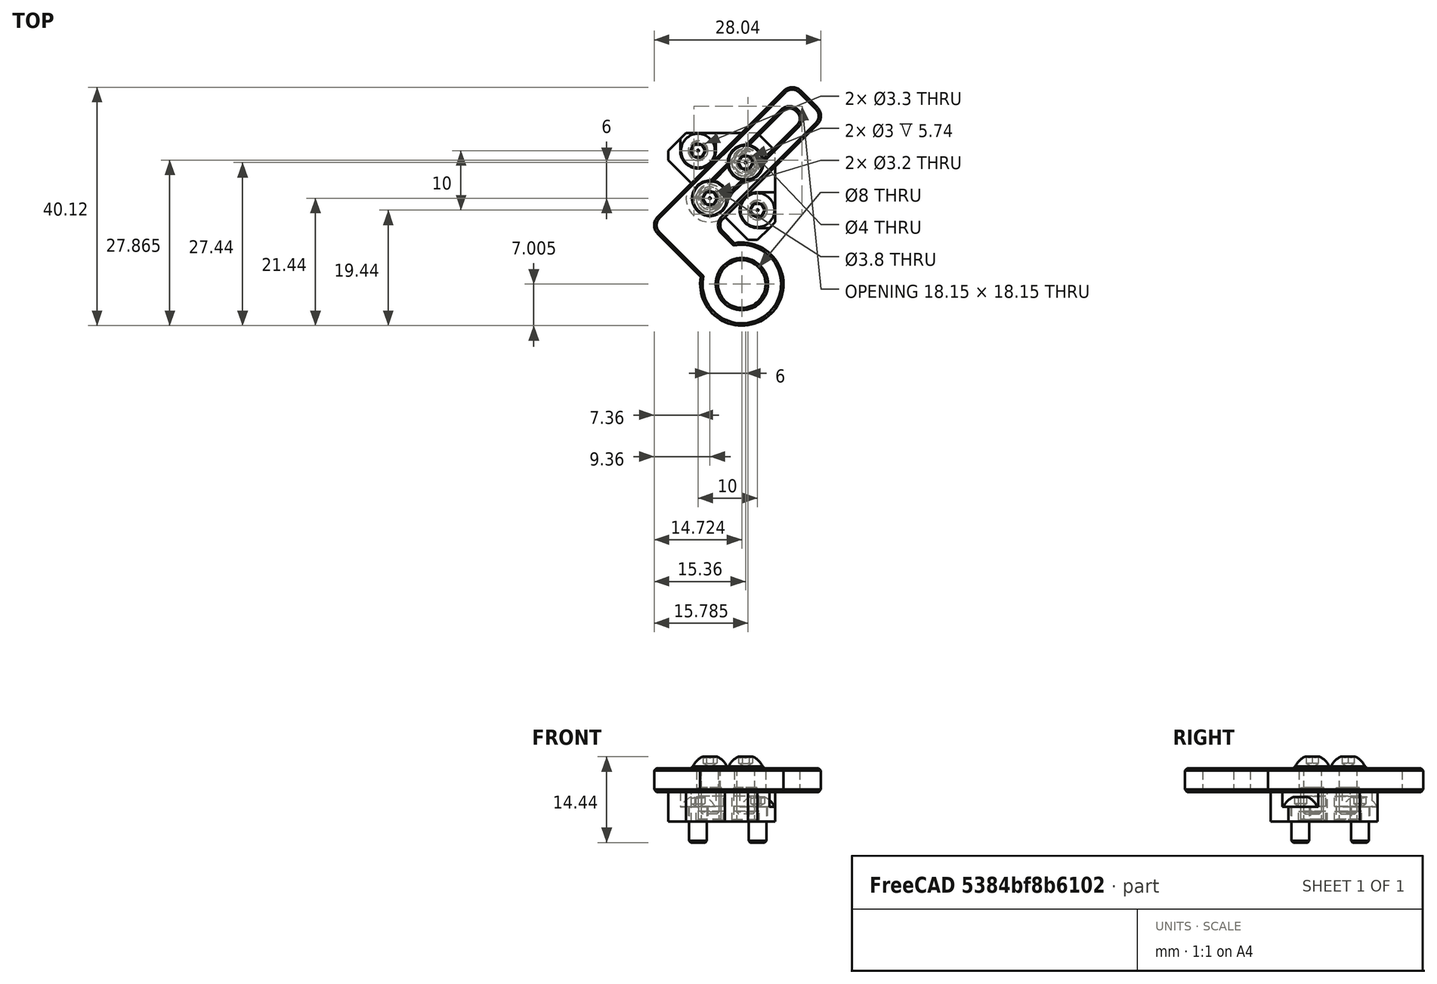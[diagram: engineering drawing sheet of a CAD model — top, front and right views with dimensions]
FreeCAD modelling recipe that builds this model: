
FCSTD DOCUMENT  (FreeCAD 0.19R24291 (Git))
Label: add-on-ptfe-tube-guide-assembly
License: Other
LicenseURL: GPL3
objects: Part::FeaturePython×8, Part::Feature×2, PartDesign::CoordinateSystem×1, App::Part×1
note: 11 computed .brp shape members not serialized (recipe doc carries the construction recipe); baked Part::Feature solids carry a one-line shape summary decoded from their .brp

FEATURE [Part::FeaturePython] Screw  label="M3x6-Screw"  # Fasteners workbench fastener (typed FeaturePython)
  Placement = pos=(-1,9,2.5) rot=(0,0,1;0rad)
  diameter = 1
  invert = true
  length = 0
  lengthCustom = 6
  matchOuter = true
  offset = 0
  thread = false
  type = 40
FEATURE [Part::FeaturePython] Screw001  label="M3x6-Screw001"  # Fasteners workbench fastener (typed FeaturePython)
  Placement = pos=(9,-1,2.5) rot=(0,0,1;0rad)
  diameter = 1
  invert = true
  length = 0
  lengthCustom = 6
  matchOuter = true
  offset = 0
  thread = false
  type = 40
FEATURE [Part::FeaturePython] HeatSet  label="M3x4-HeatSet"  # WARN: FeaturePython — macro-defined, semantics opaque (R4)
  Placement = pos=(7,7,0) rot=(-1,0,0;3.14159rad)
  diameter = 2
  invert = false
  offset = 0
FEATURE [Part::FeaturePython] Washer  label="M3-Washer"  # Fasteners workbench fastener (typed FeaturePython)
  Placement = pos=(7,7,8.74) rot=(0,0,1;0rad)
  baseObject = -> HeatSet [Edge17]
  diameter = 4
  invert = true
  matchOuter = true
  offset = 3
  type = 5
FEATURE [Part::FeaturePython] Screw002  label="M3x8-Screw"  # Fasteners workbench fastener (typed FeaturePython)
  Placement = pos=(7,7,9.29) rot=(0,0,1;0rad)
  baseObject = -> Washer [Edge1]
  diameter = 1
  invert = false
  length = 1
  lengthCustom = 8
  matchOuter = true
  offset = 0
  thread = false
  type = 40
FEATURE [PartDesign::CoordinateSystem] LCS_ptfe_tube_guide  label="LCS_ptfe-tube-guide"
  AttacherType = Attacher::AttachEngine3D
FEATURE [Part::Feature] Chamfer003002  label="ptfe-guide-base"
  shape: bbox 18 x 18 x 5 mm, 28 faces (baked)
FEATURE [Part::FeaturePython] HeatSet001  label="M3-HeatSet"  # WARN: FeaturePython — macro-defined, semantics opaque (R4)
  Placement = pos=(1,1,0) rot=(-1,0,0;3.14159rad)
  baseObject = -> Chamfer003002 [Edge69]
  diameter = 2
  invert = true
  offset = 0
FEATURE [Part::FeaturePython] Washer001  label="M3-Washer001"  # Fasteners workbench fastener (typed FeaturePython)
  Placement = pos=(1,1,8.74) rot=(0,0,1;0rad)
  baseObject = -> HeatSet001 [Edge17]
  diameter = 4
  invert = true
  matchOuter = true
  offset = 3
  type = 5
FEATURE [Part::FeaturePython] Screw003  label="M3x8-Screw001"  # Fasteners workbench fastener (typed FeaturePython)
  Placement = pos=(1,1,9.29) rot=(0,0,1;0rad)
  baseObject = -> Washer001 [Edge1]
  diameter = 1
  invert = false
  length = 1
  lengthCustom = 8
  matchOuter = true
  offset = 0
  thread = false
  type = 40
FEATURE [Part::Feature] Fusion003001002  label="ptfe-guide-arm-angle"
  Placement = pos=(-3.53553,-3.53553,9) rot=(-0.382683,-0.92388,0;3.14159rad)
  shape: bbox 28.04 x 40.11 x 4 mm, 59 faces (baked)
FEATURE [App::Part] Part  label="ptfe-tube-guide"
  Group = -> [Screw,Screw001,Chamfer003002,Washer,Screw002,LCS_ptfe_tube_guide,HeatSet001,Washer001,Screw003,Fusion003001002]
  Origin = -> Origin
